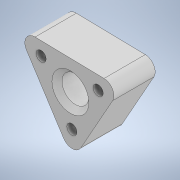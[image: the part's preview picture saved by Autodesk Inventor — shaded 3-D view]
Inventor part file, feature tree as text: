
AUTODESK INVENTOR PART (.ipt)
format: ipt  version: 2020 (Build 240168000, 168)  size: 167,424 bytes
history: native  units: mm
features: thicken_offset x3, reference x3, other x3, sketch x2, extrude x2, plane x1, chamfer x1, projected_geometry x1
ambient origin geometry x8: Origin, YZ Plane, XZ Plane, XY Plane, X Axis, Y Axis, Z Axis, Center Point
bodies: Solid1 (feature_tree)
feature tree (16):
  sketch  "Sketch1"  dims[d0=6.0mm d1=6.0mm]
  plane  "Work Plane1"
  extrude  "Extrusion1"  Depth=6.0mm
  extrude  "Extrusion2"  Depth=3.0mm
  chamfer  "Chamfer1"  Distance=3.0mm
  thicken_offset  "Thicken1"
  thicken_offset  "Thicken2"
  thicken_offset  "Thicken3"
  reference  "Reference1"
  reference  "Reference2"
  reference  "Reference3"
  sketch  "Sketch2"  dims[d2=6.0mm d3=3.0mm d4=3.0mm d5=3.0mm d6=10.0mm d7=0.0mm d8=1.0mm d9=8.0mm d10=14.0mm d11=0.0mm d12=1.5mm d13=2.0mm d14=45.0deg d15=1.0mm d16=1.0mm d17=1.0mm d18=1.0mm d19=1.0mm d20=1.0mm]
  projected_geometry  "Projected Loop1"
  parser-record x1  (decoder bookkeeping rows leaked as tree rows — omitted from the tree; the rows remain in map.json)
  other  "reducer_3.iam"
  other  "motor_h_4:1"
note: 1 file-system path scrubbed to <path> (originals preserved in map.json)
